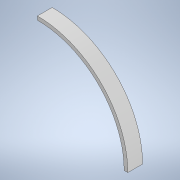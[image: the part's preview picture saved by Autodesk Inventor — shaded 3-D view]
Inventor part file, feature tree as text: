
AUTODESK INVENTOR PART (.ipt)
format: ipt  version: 2021 (Build 250183000, 183)  size: 100,352 bytes
history: native  units: in
note: dims shown in document units (in); Inventor stores cm internally (conversion verified against a paired STEP export)
features: extrude x1, sketch x1
ambient origin geometry x8: Origin, YZ Plane, XZ Plane, XY Plane, X Axis, Y Axis, Z Axis, Center Point
bodies: Solid1 (feature_tree)
feature tree (2):
  extrude  "Extrusion1"  Depth=1.0in
  sketch  "Sketch1"  dims[d0=11.75in d1=12.25in d3=1.0in d4=0.0in]
